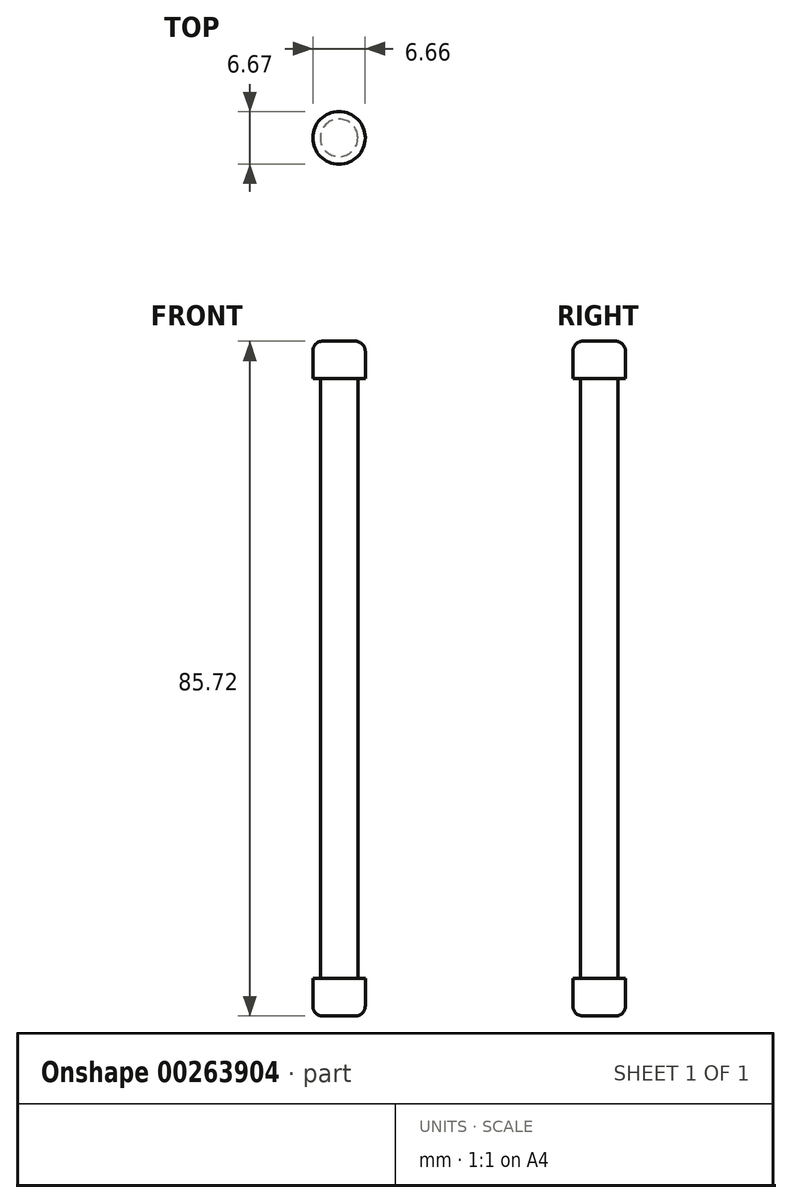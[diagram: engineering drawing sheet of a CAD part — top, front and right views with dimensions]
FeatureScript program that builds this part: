
annotation { "Feature Type Name" : "Feature", "Feature Type Description" : "" }
export const myFeature = defineFeature(function(context is Context, id is Id, definition is map)
    precondition{}
    {
        {
            var Q0;
            Q0=qCreatedBy(makeId("Top.planeOp"),FACE);
            var sketch = newSketch(context, id + "F0", { "sketchPlane" : qUnion([Q0])});
            skCircle(sketch, "E0", {"center": v(-29.11, -9.7) * mm, "radius": 2.38 * mm});
            skSolve(sketch);
        }
        {
            var Q0;
            Q0 = qSketchRegion(id + "F0", true);
            extrude(context, id + "F1", {"entities" : qUnion([Q0]), "depth" : 76.2 * mm});
        }
        {
            var Q0;
            Q0=makeQuery(id+"F1.opExtrude","CAP_FACE",FACE,{"disambiguationData":[OSD([sQuery(id+"F0.wireOp",EDGE,"E0")])],"isStart":false});
            var sketch = newSketch(context, id + "F2", { "sketchPlane" : qUnion([Q0])});
            skCircle(sketch, "E1", {"center": v(-29.11, -9.7) * mm, "radius": 3.33 * mm});
            skSolve(sketch);
        }
        {
            var Q0;
            Q0 = qSketchRegion(id + "F2", true);
            extrude(context, id + "F3", {"entities" : qUnion([Q0]), "operationType" : NewBodyOperationType.ADD, "depth" : 4.76 * mm});
        }
        {
            var Q0;
            Q0=makeQuery(id+"F1.opExtrude","CAP_FACE",FACE,{"disambiguationData":[OSD([sQuery(id+"F0.wireOp",EDGE,"E0")])],"isStart":true});
            var sketch = newSketch(context, id + "F4", { "sketchPlane" : qUnion([Q0])});
            skCircle(sketch, "E2", {"center": v(-29.11, 9.7) * mm, "radius": 3.33 * mm});
            skSolve(sketch);
        }
        {
            var Q0;
            Q0 = qSketchRegion(id + "F4", true);
            extrude(context, id + "F5", {"entities" : qUnion([Q0]), "operationType" : NewBodyOperationType.ADD, "depth" : 4.76 * mm});
        }
        {
            var Q0;
            Q0=makeQuery(id+"F5.opExtrude","CAP_EDGE",EDGE,{"disambiguationData":[OSD([sQuery(id+"F4.wireOp",EDGE,"E2")])],"isStart":false});
            fillet(context, id + "F6", {"entities" : qUnion([Q0]), "radius" : 1.27 * mm, "tangentPropagation" : true, "allowEdgeOverflow" : false});
        }
        {
            var Q0;
            Q0=makeQuery(id+"F3.opExtrude","CAP_EDGE",EDGE,{"disambiguationData":[OSD([sQuery(id+"F2.wireOp",EDGE,"E1")])],"isStart":false});
            fillet(context, id + "F7", {"entities" : qUnion([Q0]), "radius" : 1.27 * mm, "tangentPropagation" : true, "allowEdgeOverflow" : false});
        }
    });
